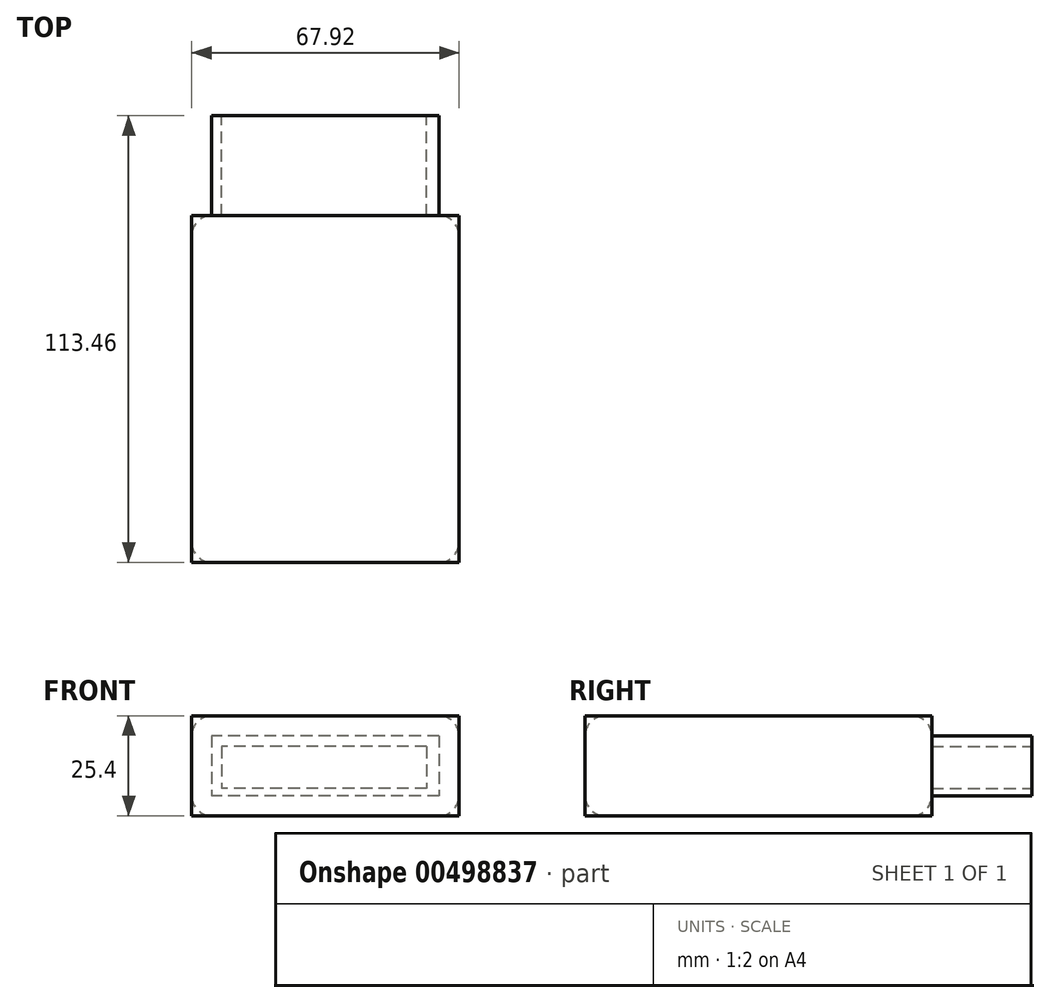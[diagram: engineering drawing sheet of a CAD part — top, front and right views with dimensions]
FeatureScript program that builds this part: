
annotation { "Feature Type Name" : "Feature", "Feature Type Description" : "" }
export const myFeature = defineFeature(function(context is Context, id is Id, definition is map)
    precondition{}
    {
        {
            var Q0;
            Q0=qCreatedBy(makeId("Top.planeOp"),FACE);
            var sketch = newSketch(context, id + "F0", { "sketchPlane" : qUnion([Q0])});
            skLineSegment(sketch, "E0.bottom", {"start": v(33.96, 44.03) * mm, "end": v(-33.96, 44.03) * mm});
            skLineSegment(sketch, "E0.top", {"start": v(33.96, -44.03) * mm, "end": v(-33.96, -44.03) * mm});
            skLineSegment(sketch, "E0.left", {"start": v(33.96, 44.03) * mm, "end": v(33.96, -44.03) * mm});
            skLineSegment(sketch, "E0.right", {"start": v(-33.96, 44.03) * mm, "end": v(-33.96, -44.03) * mm});
            skPoint(sketch, "E0.middle", {"position": v(0, 0) * mm});
            skSolve(sketch);
        }
        {
            var Q0;
            Q0=makeQuery(id+"F0.imprint","IMPRINT",FACE,{"disambiguationData":[TD([[makeQuery(id+"F0.imprint","IMPRINT",EDGE,{"derivedFrom":sQuery(id+"F0.wireOp",EDGE,"E0.bottom")}),1.0]])]});
            extrude(context, id + "F1", {"entities" : qUnion([Q0]), "depth" : 25.4 * mm});
        }
        {
            var Q0;
            Q0=makeQuery(id+"F1.opExtrude","SWEPT_FACE",FACE,{"disambiguationData":[OSD([sQuery(id+"F0.wireOp",EDGE,"E0.left")])]});
            var Q1;
            Q1=makeQuery(id+"F1.opExtrude","SWEPT_FACE",FACE,{"disambiguationData":[OSD([sQuery(id+"F0.wireOp",EDGE,"E0.top")])]});
            var Q2;
            Q2=makeQuery(id+"F1.opExtrude","SWEPT_FACE",FACE,{"disambiguationData":[OSD([sQuery(id+"F0.wireOp",EDGE,"E0.right")])]});
            var Q3;
            Q3=makeQuery(id+"F1.opExtrude","SWEPT_FACE",FACE,{"disambiguationData":[OSD([sQuery(id+"F0.wireOp",EDGE,"E0.bottom")])]});
            fillet(context, id + "F2", {"entities" : qUnion([Q0, Q1, Q2, Q3]), "radius" : 5.08 * mm, "tangentPropagation" : true, "allowEdgeOverflow" : false});
        }
        {
            var Q0;
            Q0=makeQuery(id+"F1.opExtrude","SWEPT_FACE",FACE,{"disambiguationData":[OSD([sQuery(id+"F0.wireOp",EDGE,"E0.bottom")])]});
            extrude(context, id + "F3", {"entities" : qUnion([Q0]), "operationType" : NewBodyOperationType.ADD, "depth" : 25.4 * mm});
        }
        {
            var Q0;
            Q0=makeQuery(id+"F3.opExtrude","CAP_FACE",FACE,{"disambiguationData":[OSD([sQuery(id+"F0.wireOp",EDGE,"E0.bottom")])],"isStart":false});
            var sketch = newSketch(context, id + "F4", { "sketchPlane" : qUnion([Q0])});
            skLineSegment(sketch, "E1.bottom", {"start": v(-25.74, 17.61) * mm, "end": v(26.34, 17.61) * mm});
            skLineSegment(sketch, "E1.top", {"start": v(-25.74, 6.98) * mm, "end": v(26.34, 6.98) * mm});
            skLineSegment(sketch, "E1.left", {"start": v(-25.74, 17.61) * mm, "end": v(-25.74, 6.98) * mm});
            skLineSegment(sketch, "E1.right", {"start": v(26.34, 17.61) * mm, "end": v(26.34, 6.98) * mm});
            skSolve(sketch);
        }
        {
            var Q0;
            Q0 = qSketchRegion(id + "F4", true);
            extrude(context, id + "F5", {"entities" : qUnion([Q0]), "operationType" : NewBodyOperationType.REMOVE, "oppositeDirection" : true, "depth" : 25.4 * mm, "offsetDistance" : 25.4 * mm});
        }
        {
            var Q0;
            Q0=makeQuery(id+"F0.imprint","IMPRINT",FACE,{"disambiguationData":[TD([[makeQuery(id+"F0.imprint","IMPRINT",EDGE,{"derivedFrom":sQuery(id+"F0.wireOp",EDGE,"E0.bottom")}),1.0]])]});
            extrude(context, id + "F6", {"entities" : qUnion([Q0]), "depth" : 25.4 * mm});
        }
    });
